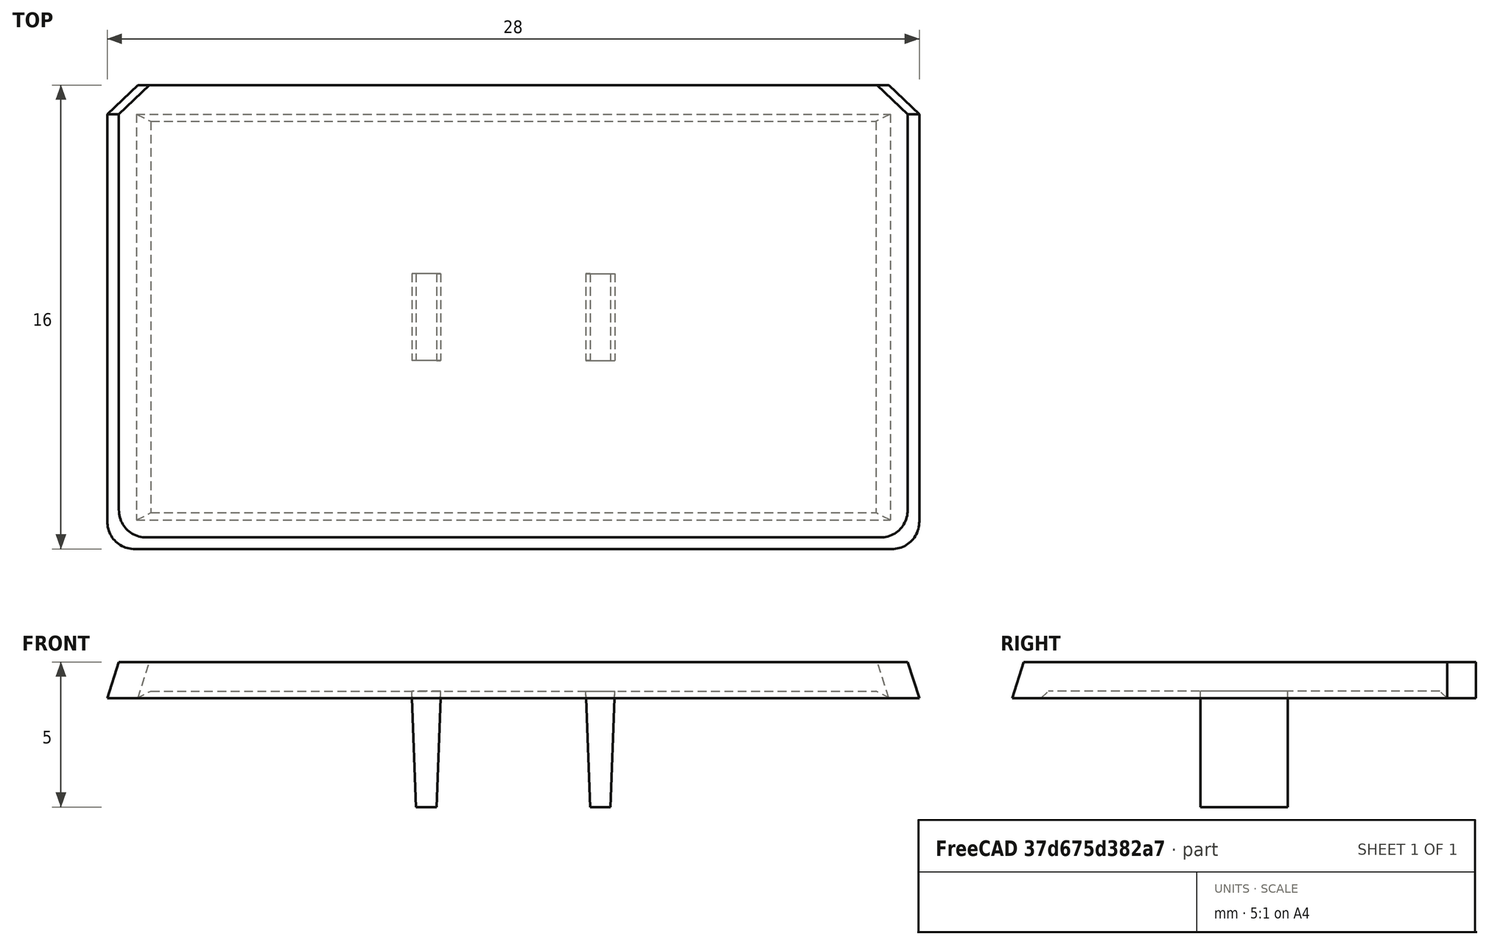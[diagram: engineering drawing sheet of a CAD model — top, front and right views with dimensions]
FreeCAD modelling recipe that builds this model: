
FCSTD DOCUMENT  (FreeCAD 0.20R27078 (Git))
Label: kailh_keycap
License: All rights reserved
LicenseURL: http://en.wikipedia.org/wiki/All_rights_reserved
objects: PartDesign::AdditiveWedge×2, Spreadsheet::Sheet×1, PartDesign::Chamfer×1, PartDesign::Fillet×1, PartDesign::SubtractiveWedge×1, PartDesign::Mirrored×1, PartDesign::Body×1
note: 12 computed .brp shape members not serialized (recipe doc carries the construction recipe); baked Part::Feature solids carry a one-line shape summary decoded from their .brp

FEATURE [Spreadsheet::Sheet] Spreadsheet
  cells = B2=key size; C2(units)=1.5; D2=unit
FEATURE [PartDesign::AdditiveWedge] Wedge  label="Cap"
  AttacherType = Attacher::AttachEngine3D
  AttachmentOffset = pos=(0,0,0) rot=(1,0,0;1.5708rad)
  MapMode = 5
  Placement = pos=(0,0,0) rot=(1,0,0;1.5708rad)
  Support = -> [XY_Plane]
  X2max = 13.6
  X2min = -13.6
  Xmax = 14
  Xmin = -14
  Ymax = 1.25
  Ymin = 0
  Z2max = 7.6
  Z2min = -8
  Zmax = 8
  Zmin = -8
  expr: X2max = Xmax - 0.4mm
  expr: X2min = -X2max
  expr: Xmax = Spreadsheet.units * 12mm - 4mm
  expr: Xmin = -Xmax
FEATURE [PartDesign::Chamfer] Chamfer  label="TopChamfer"
  Angle = 45
  Base = -> Wedge [Edge8,Edge4]
  BaseFeature = -> Wedge
  ChamferType = 0
  FlipDirection = false
  Placement = pos=(0,0,0) rot=(1,0,0;1.5708rad)
  Size = 1
  Size2 = 1
  SupportTransform = false
FEATURE [PartDesign::Fillet] Fillet
  Base = -> Chamfer [Edge3,Edge13]
  BaseFeature = -> Chamfer
  Placement = pos=(0,0,0) rot=(1,0,0;1.5708rad)
  Radius = 1
  SupportTransform = false
FEATURE [PartDesign::SubtractiveWedge] Wedge002  label="InnerSpace"
  AttacherType = Attacher::AttachEngine3D
  AttachmentOffset = pos=(0,0,0) rot=(1,0,0;1.5708rad)
  BaseFeature = -> Fillet
  MapMode = 5
  Placement = pos=(0,0,0) rot=(1,0,0;1.5708rad)
  Support = -> [XY_Plane]
  X2max = 12.5
  X2min = -12.5
  Xmax = 13
  Xmin = -13
  Ymax = 0.25
  Ymin = 0
  Z2max = 6.75
  Z2min = -6.75
  Zmax = 7
  Zmin = -7
  expr: X2max = Xmax - 0.5mm
  expr: X2min = -X2max
  expr: Xmax = <<Cap>>.Xmax - 1mm
  expr: Xmin = -Xmax
  expr: Z2min = -Z2max
  expr: Zmin = -Zmax
FEATURE [PartDesign::AdditiveWedge] Wedge001  label="Leg"
  AttacherType = Attacher::AttachEngine3D
  AttachmentOffset = pos=(2.5,1.5,0.25) rot=(1,0,0;1.5708rad)
  BaseFeature = -> Wedge002
  MapMode = 5
  Placement = pos=(2.5,1.5,0.25) rot=(1,0,0;1.5708rad)
  Support = -> [XY_Plane]
  X2max = 1
  X2min = 0
  Xmax = 0.85
  Xmin = 0.15
  Ymax = 0
  Ymin = -4
  Z2max = 3
  Z2min = 0
  Zmax = 3
  Zmin = 0
  expr: .AttachmentOffset.Base.y = Zmax / 2
FEATURE [PartDesign::Mirrored] Mirrored
  BaseFeature = -> Wedge001
  MirrorPlane = -> YZ_Plane
  Originals = -> [Wedge001]
  Overlap = 0
  Placement = pos=(2.5,1.5,0.25) rot=(1,0,0;1.5708rad)
FEATURE [PartDesign::Body] Body  label="KeyCap"
  Group = -> [Wedge,Chamfer,Fillet,Wedge002,Wedge001,Mirrored]
  Origin = -> Origin
  Tip = -> Mirrored
